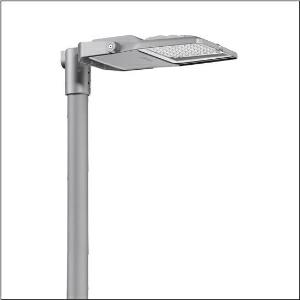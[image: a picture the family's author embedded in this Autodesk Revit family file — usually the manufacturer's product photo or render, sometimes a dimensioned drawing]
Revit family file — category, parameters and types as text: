
# Revit family: floodlight_fl_21_iq_mini___pl43_5xa7772c4a3a_a38e
name_source: partatom
category: Lighting Fixtures
units: mm (PartAtom-declared; Revit-internal decimal feet)

## family parameters
Cut with Voids When Loaded = No
Host = Face
Light Source = No
Part Type = Normal
Room Calculation Point = No
Round Connector Dimension = Use Diameter
Shared = No

## types (1)
- --- (1 x LED, 13050 lm, 87.2 W, 4000K)
    Apparent Load = 87 VA
    CIE Flux Codes = 27 78 99 100 100
    Color Rendering = 70
    Color Temperature = 4000K
    Default Elevation = 1800 mm
    Description = Floodlight FL 21 iQ mini, floodlight, primary light control with lens, of PMMA, primary optical cover: protective disc, of toughened safety glass, transparent, light distribution: PL43, light emission: direct distribution, installation type: surface-mounted, LED, High Power LED, rated luminous flux: 13.050lm, luminous efficacy: 150lm/W, light colour: 740, colour temperature: 4000K, control: Auto-Match, Temp-Guard, Night-Set, Smart-Wire, Desk-Remote (wireless, voltage-free reading and setting of iQ features in the workshop via application-optimized NFC function/RFID function), optimised constant luminous flux control (CLO 2.0), Light-Fading, Lumen-Switch, with terminal, 6-pole, mains connection: 220..240V, AC, 50/60Hz, start of lifetime: 87W, end of service life: 92W, reduction: 40W, luminaire housing, of diecast aluminium, powder-coated, Siteco® metallic grey (DB 702S), corrosivity category C5 mid according to DIN EN ISO 12944, sealing non-destructively replaceable, please order mast flange separately, mast bracket, of steel, galvanised, powder-coated, protection rating (complete): IP66, insulation class (complete): insulation class II (safety insulation), certification: CE, ENEC, VDE, protection symbol: D, impact resistance: IK08, permissible operating ambient temperature: -40..+40°C, permissible operating ambient temperature for outdoor applications: -40..+50°C, standard: DIN EN 12944, LABS conformity tested according to VDMA 24364:2018-05, packaging unit: 1 piece

Light Distribution: PL43
    Height = 70 mm
    Lamp = 1 x LED
    Lamp Light Flux = 13050 lm
    Lamp Power = 87.2 W
    Lamp count = 1
    Length = 485 mm
    Luminous efficacy = 150 lm/W
    Manufacturer = Siteco
    ModVariant = No
    Model = 5XA7772C4A3A
    Number of Poles = 1
    OnlyDefault = Yes
    Power Factor = 1
    Product Name = Floodlight FL 21 iQ mini | PL43
    Product group = floodlight | pylon annexe
    ProductGroupID = 6200
    Protection Class = Protection class II
    Protection Degree = IP 66
    RLX_Detail_Level = 1
    RLX_Emergency_Light_Flux = 0 lm
    RLX_Emergency_Type = 0
    RLX_Emergency_Type_DB = No
    RlxData = <blob elided: 101293 chars, md5=54d914cd>
    Socket = socket
    Standby Power = 0 W
    System Light Flux = 13050 lm
    System Power = 87 W
    Type Comments = factory setting: luminous flux: 100 % | dim-lin: 254 | 456 mA
    Type Image = l_1007125.jpg
    URL = http://relux.com
    VarID = @adj_132495
    Voltage = 0 V
    Weight = 0.00 kg
    Width = 337 mm

## geometry (parser evidence)
native form markers: Blend x4, Sweep x13
no freeform markers — native parametric forms only
